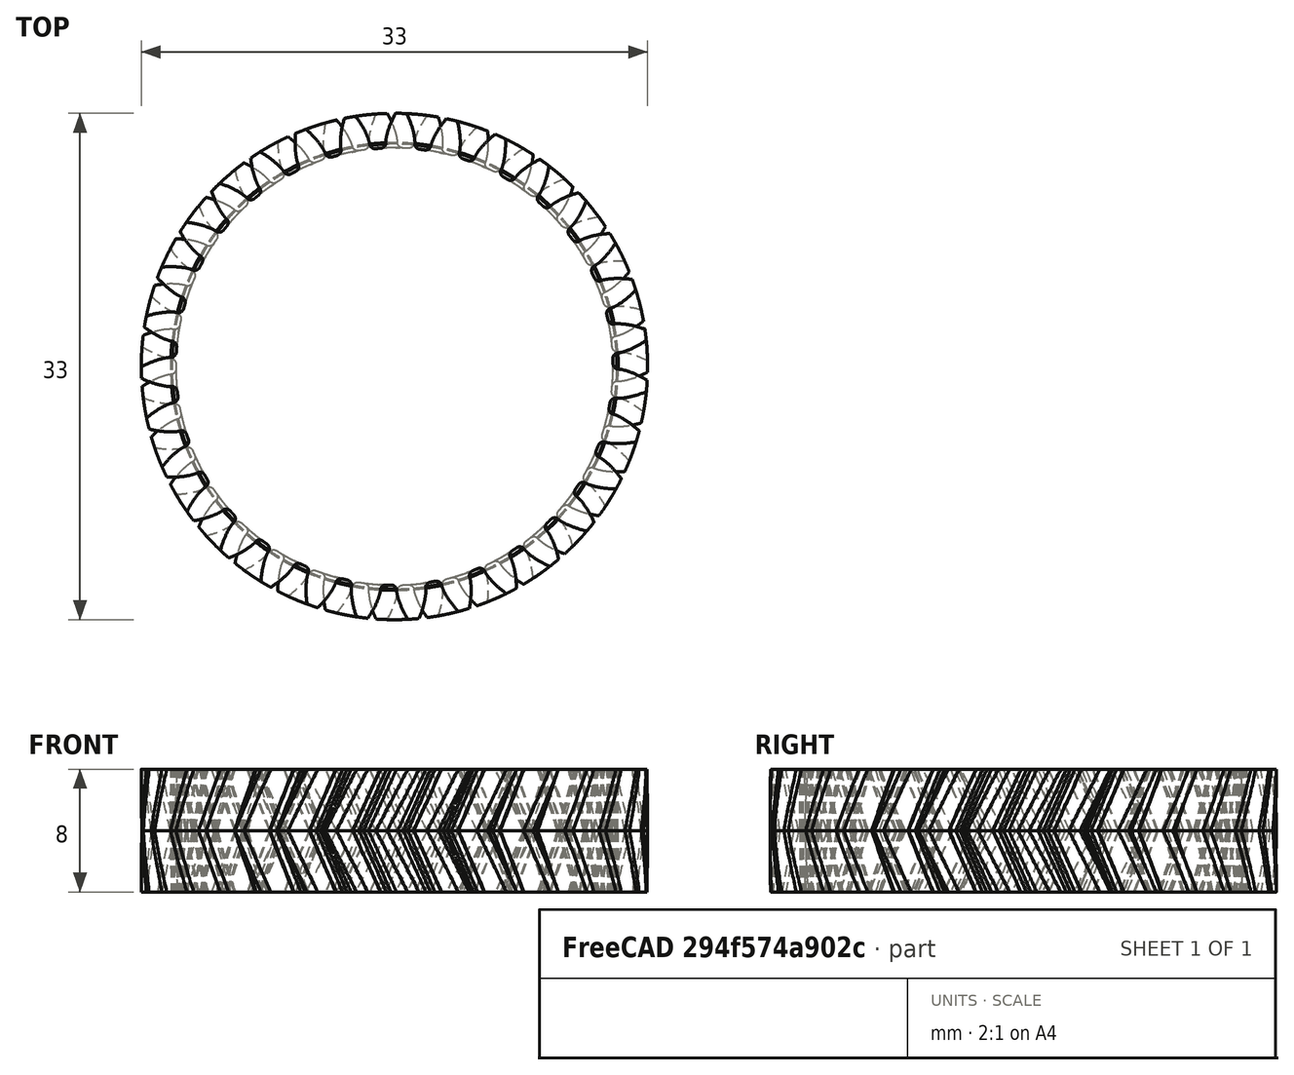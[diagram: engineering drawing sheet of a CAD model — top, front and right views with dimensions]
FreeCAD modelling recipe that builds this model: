
FCSTD DOCUMENT  (FreeCAD 0.17R13541 (Git))
Label: Gear5
License: All rights reserved
LicenseURL: http://en.wikipedia.org/wiki/All_rights_reserved
objects: Part::Helix×2, Part::Sweep×2, Part::Part2DObjectPython×1
note: 5 computed .brp shape members not serialized (recipe doc carries the construction recipe); baked Part::Feature solids carry a one-line shape summary decoded from their .brp

FEATURE [Part::Part2DObjectPython] InvoluteGear  # Draft 2D object (typed FeaturePython)
  ExternalGear = true
  HighPrecision = true
  Modules = 1
  NumberOfTeeth = 31
  PressureAngle = 20
FEATURE [Part::Helix] Helix002
  Angle = 0
  AttacherType = Attacher::AttachEngine3D
  Height = 4
  LocalCoord = 0
  Pitch = 200
  Radius = 16.5
  Style = 1
FEATURE [Part::Sweep] Sweep
  Frenet = true
  Sections = -> [InvoluteGear]
  Solid = true
  Spine = -> Helix002 [Edge1]
  Transition = 1
FEATURE [Part::Helix] Helix
  Angle = 0
  AttacherType = Attacher::AttachEngine3D
  Height = 4
  LocalCoord = 1
  Pitch = 200
  Placement = pos=(0,0,0) rot=(1,0,0;3.14159rad)
  Radius = 16.5
  Style = 1
FEATURE [Part::Sweep] Sweep001
  Frenet = true
  Sections = -> [InvoluteGear]
  Solid = true
  Spine = -> Helix [Edge1]
  Transition = 1
